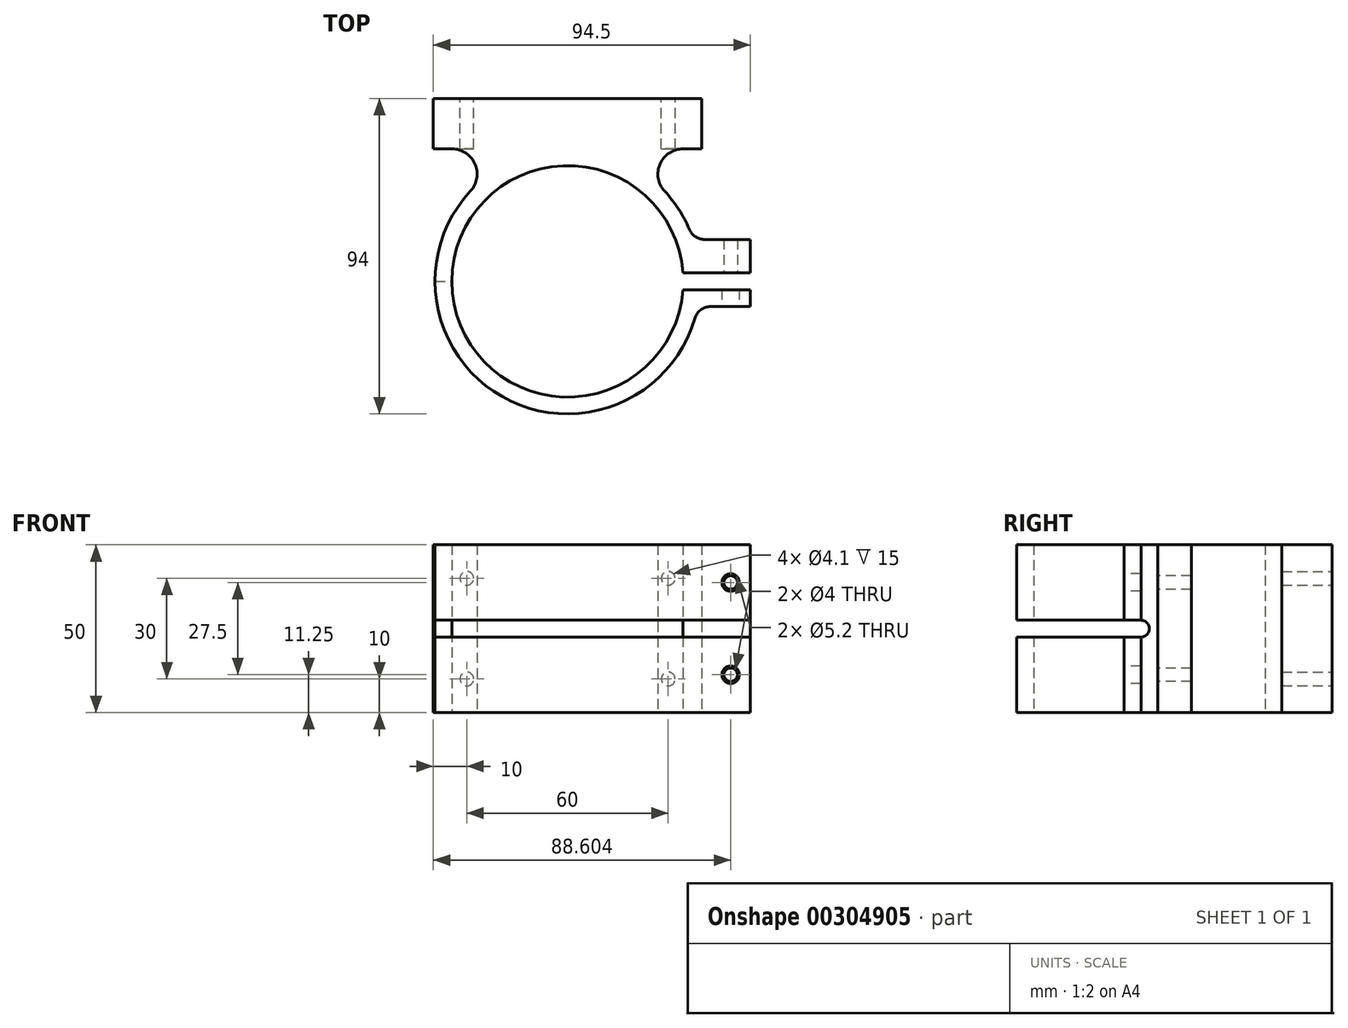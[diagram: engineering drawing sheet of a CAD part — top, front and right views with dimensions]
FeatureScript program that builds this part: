
annotation { "Feature Type Name" : "Feature", "Feature Type Description" : "" }
export const myFeature = defineFeature(function(context is Context, id is Id, definition is map)
    precondition{}
    {
        {
            var Q0;
            Q0=qCreatedBy(makeId("Top.planeOp"),FACE);
            var sketch = newSketch(context, id + "F0", { "sketchPlane" : qUnion([Q0])});
            skArc(sketch, "E0", {"start": v(34.4, 2.5) * mm, "mid": v(-34.5, 0) * mm, "end": v(34.4, -2.5) * mm});
            skArc(sketch, "E1", {"start": v(36.32, 15.53) * mm, "mid": v(33.11, 21.53) * mm, "end": v(28.93, 26.9) * mm});
            skLineSegment(sketch, "E2.bottom", {"start": v(40, 39.5) * mm, "end": v(34.42, 39.5) * mm});
            skLineSegment(sketch, "E2.top", {"start": v(40, 54.5) * mm, "end": v(-40, 54.5) * mm});
            skLineSegment(sketch, "E2.left", {"start": v(40, 39.5) * mm, "end": v(40, 54.5) * mm});
            skLineSegment(sketch, "E2.right", {"start": v(-40, 39.5) * mm, "end": v(-40, 54.5) * mm});
            skPoint(sketch, "E2.middle", {"position": v(0, 47) * mm});
            skLineSegment(sketch, "E3", {"start": v(0, 54.5) * mm, "end": v(0, 34.5) * mm});
            skLineSegment(sketch, "E4.bottom", {"start": v(54.5, -2.5) * mm, "end": v(34.4, -2.5) * mm});
            skLineSegment(sketch, "E4.top", {"start": v(54.5, 2.5) * mm, "end": v(34.4, 2.5) * mm});
            skLineSegment(sketch, "E4.right", {"start": v(14.5, -2.5) * mm, "end": v(14.5, 2.5) * mm});
            skPoint(sketch, "E4.middle", {"position": v(34.5, 0) * mm});
            skLineSegment(sketch, "E5.bottom", {"start": v(54.5, -7.5) * mm, "end": v(42.7, -7.5) * mm});
            skLineSegment(sketch, "E5.left", {"start": v(54.5, -7.5) * mm, "end": v(54.5, -2.5) * mm});
            skLineSegment(sketch, "E5.right", {"start": v(14.5, -7.5) * mm, "end": v(14.5, 7.5) * mm});
            skLineSegment(sketch, "E6.trimOffspring", {"start": v(54.5, 2.5) * mm, "end": v(54.5, 7.5) * mm});
            skPoint(sketch, "E7.visualSharp", {"position": v(38.78, 7.5) * mm});
            skPoint(sketch, "E8.visualSharp", {"position": v(38.78, -7.5) * mm});
            skArc(sketch, "E8.filletArc", {"start": v(42.7, -7.5) * mm, "mid": v(39.71, -8.5) * mm, "end": v(37.9, -11.1) * mm});
            skArc(sketch, "E9.trimOffspring", {"start": v(-28.93, 26.9) * mm, "mid": v(-19.52, -34.34) * mm, "end": v(37.9, -11.1) * mm});
            skLineSegment(sketch, "E10.trimOffspring", {"start": v(-34.42, 39.5) * mm, "end": v(-40, 39.5) * mm});
            skArc(sketch, "E11.filletArc", {"start": v(-28.93, 26.9) * mm, "mid": v(-27.55, 35) * mm, "end": v(-34.42, 39.5) * mm});
            skArc(sketch, "E12.filletArc", {"start": v(34.42, 39.5) * mm, "mid": v(27.55, 35) * mm, "end": v(28.93, 26.9) * mm});
            skLineSegment(sketch, "E13.top", {"start": v(54.5, 12.5) * mm, "end": v(40.91, 12.5) * mm});
            skLineSegment(sketch, "E13.left", {"start": v(54.5, 7.5) * mm, "end": v(54.5, 12.5) * mm});
            skPoint(sketch, "E14.visualSharp", {"position": v(37.47, 12.5) * mm});
            skArc(sketch, "E14.filletArc", {"start": v(36.32, 15.53) * mm, "mid": v(38.16, 13.33) * mm, "end": v(40.91, 12.5) * mm});
            skSolve(sketch);
        }
        {
            var Q0;
            {var subQ3=sQuery(id+"F0.wireOp",EDGE,"E2.right");Q0=makeQuery(id+"F0.imprint","IMPRINT",FACE,{"disambiguationData":[TD([[makeQuery(id+"F0.imprint","IMPRINT",EDGE,{"derivedFrom":subQ3}),-1.0]])]});}
            var Q1;
            Q1=makeQuery(id+"F0.imprint","IMPRINT",FACE,{"disambiguationData":[TD([[makeQuery(id+"F0.imprint","IMPRINT",EDGE,{"derivedFrom":sQuery(id+"F0.wireOp",EDGE,"E1")}),1.0]])]});
            extrude(context, id + "F1", {"entities" : qUnion([Q0, Q1]), "depth" : 50 * mm});
        }
        {
            var Q0;
            Q0=makeQuery(id+"F1.opExtrude","SWEPT_FACE",FACE,{"disambiguationData":[OSD([sQuery(id+"F0.wireOp",EDGE,"E2.top")])]});
            var sketch = newSketch(context, id + "F2", { "sketchPlane" : qUnion([Q0])});
            skLineSegment(sketch, "E15", {"start": v(-40, 10) * mm, "end": v(40, 10) * mm, "construction": true});
            skLineSegment(sketch, "E16", {"start": v(-40, 40) * mm, "end": v(40, 40) * mm, "construction": true});
            skCircle(sketch, "E17", {"center": v(-30, 10) * mm, "radius": 2.05 * mm});
            skCircle(sketch, "E18", {"center": v(-30, 40) * mm, "radius": 2.05 * mm});
            skCircle(sketch, "E19", {"center": v(30, 40) * mm, "radius": 2.05 * mm});
            skCircle(sketch, "E20", {"center": v(30, 10) * mm, "radius": 2.05 * mm});
            skSolve(sketch);
        }
        {
            var Q0;
            Q0 = qSketchRegion(id + "F2", true);
            extrude(context, id + "F3", {"entities" : qUnion([Q0]), "operationType" : NewBodyOperationType.REMOVE, "oppositeDirection" : true, "depth" : 15 * mm});
        }
        {
            var Q0;
            Q0=qCreatedBy(makeId("Front.planeOp"),FACE);
            var sketch = newSketch(context, id + "F4", { "sketchPlane" : qUnion([Q0])});
            skLineSegment(sketch, "E21", {"start": v(0, 25) * mm, "end": v(57.85, 25) * mm});
            skArc(sketch, "E22.0.startCap", {"start": v(0, 22.5) * mm, "mid": v(-2.5, 25) * mm, "end": v(0, 27.5) * mm});
            skArc(sketch, "E22.0.endCap", {"start": v(57.85, 27.5) * mm, "mid": v(60.35, 25) * mm, "end": v(57.85, 22.5) * mm});
            skLineSegment(sketch, "E22.0.left", {"start": v(0, 27.5) * mm, "end": v(57.85, 27.5) * mm});
            skLineSegment(sketch, "E22.0.right", {"start": v(0, 22.5) * mm, "end": v(57.85, 22.5) * mm});
            skSolve(sketch);
        }
        {
            var Q0;
            {var subQ2=sQuery(id+"F0.wireOp",EDGE,"E5.bottom");Q0=makeQuery(id+"FSlxkKbNy0vXjha_1.boolean.opBoolean","SPLIT",FACE,{"disambiguationData":[TD([makeQuery(id+"FSlxkKbNy0vXjha_1.opExtrude","SWEPT_FACE",FACE,{"disambiguationData":[OSD([sQuery(id+"F4.wireOp",EDGE,"E22.0.left")])]})])],"derivedFrom":makeQuery(id+"F1.opExtrude","SWEPT_FACE",FACE,{"disambiguationData":[OSD([subQ2])]})});}
            var sketch = newSketch(context, id + "F5", { "sketchPlane" : qUnion([Q0])});
            skLineSegment(sketch, "E23", {"start": v(48.6, 50) * mm, "end": v(48.6, 0) * mm, "construction": true});
            skLineSegment(sketch, "E24", {"start": v(54.5, 11.25) * mm, "end": v(42.7, 11.25) * mm, "construction": true});
            skCircle(sketch, "E25", {"center": v(48.6, 38.75) * mm, "radius": 2.6 * mm});
            skCircle(sketch, "E26", {"center": v(48.6, 11.25) * mm, "radius": 2.6 * mm});
            skCircle(sketch, "E27", {"center": v(48.6, 38.75) * mm, "radius": 2 * mm});
            skCircle(sketch, "E28", {"center": v(48.6, 11.25) * mm, "radius": 2 * mm});
            skSolve(sketch);
        }
        {
            var Q0;
            Q0=makeQuery(id+"F5.imprint","IMPRINT",FACE,{"disambiguationData":[TD([[makeQuery(id+"F5.imprint","IMPRINT",EDGE,{"derivedFrom":sQuery(id+"F5.wireOp",EDGE,"E28")}),1.0]])]});
            var Q1;
            Q1=makeQuery(id+"F5.imprint","IMPRINT",FACE,{"disambiguationData":[TD([[makeQuery(id+"F5.imprint","IMPRINT",EDGE,{"derivedFrom":sQuery(id+"F5.wireOp",EDGE,"E27")}),1.0]])]});
            extrude(context, id + "F6", {"entities" : qUnion([Q0, Q1]), "operationType" : NewBodyOperationType.REMOVE, "endBound" : BoundingType.THROUGH_ALL, "oppositeDirection" : true, "depth" : 25 * mm});
        }
        {
            var Q0;
            Q0=makeQuery(id+"F5.imprint","IMPRINT",FACE,{"disambiguationData":[TD([[makeQuery(id+"F5.imprint","IMPRINT",EDGE,{"derivedFrom":sQuery(id+"F5.wireOp",EDGE,"E26")}),1.0]])]});
            var Q1;
            Q1=makeQuery(id+"F5.imprint","IMPRINT",FACE,{"disambiguationData":[TD([[makeQuery(id+"F5.imprint","IMPRINT",EDGE,{"derivedFrom":sQuery(id+"F5.wireOp",EDGE,"E25")}),1.0]])]});
            var Q2;
            {var subQ2=sQuery(id+"F0.wireOp",EDGE,"E4.bottom");Q2=makeQuery(id+"FSlxkKbNy0vXjha_1.boolean.opBoolean","SPLIT",FACE,{"disambiguationData":[TD([makeQuery(id+"FSlxkKbNy0vXjha_1.opExtrude","SWEPT_FACE",FACE,{"disambiguationData":[OSD([sQuery(id+"F4.wireOp",EDGE,"E22.0.right")])]})])],"derivedFrom":makeQuery(id+"F1.opExtrude","SWEPT_FACE",FACE,{"disambiguationData":[OSD([subQ2])]})});}
            extrude(context, id + "F7", {"entities" : qUnion([Q0, Q1]), "operationType" : NewBodyOperationType.REMOVE, "endBound" : BoundingType.UP_TO_SURFACE, "oppositeDirection" : true, "endBoundEntityFace" : qUnion([Q2]), "depth" : 25 * mm});
        }
        {
            var Q0;
            Q0=qCreatedBy(makeId("Right.planeOp"),FACE);
            var sketch = newSketch(context, id + "F8", { "sketchPlane" : qUnion([Q0])});
            skLineSegment(sketch, "E29", {"start": v(-2.5, 25) * mm, "end": v(-48.95, 25) * mm});
            skArc(sketch, "E30.0.startCap", {"start": v(-2.5, 27.5) * mm, "mid": v(0, 25) * mm, "end": v(-2.5, 22.5) * mm});
            skArc(sketch, "E30.0.endCap", {"start": v(-48.95, 22.5) * mm, "mid": v(-51.45, 25) * mm, "end": v(-48.95, 27.5) * mm});
            skLineSegment(sketch, "E30.0.left", {"start": v(-2.5, 22.5) * mm, "end": v(-48.95, 22.5) * mm});
            skLineSegment(sketch, "E30.0.right", {"start": v(-2.5, 27.5) * mm, "end": v(-48.95, 27.5) * mm});
            skSolve(sketch);
        }
        {
            var Q0;
            Q0 = qSketchRegion(id + "F8", true);
            extrude(context, id + "F9", {"entities" : qUnion([Q0]), "operationType" : NewBodyOperationType.REMOVE, "endBound" : BoundingType.SYMMETRIC, "oppositeDirection" : true, "depth" : 200 * mm});
        }
    });
